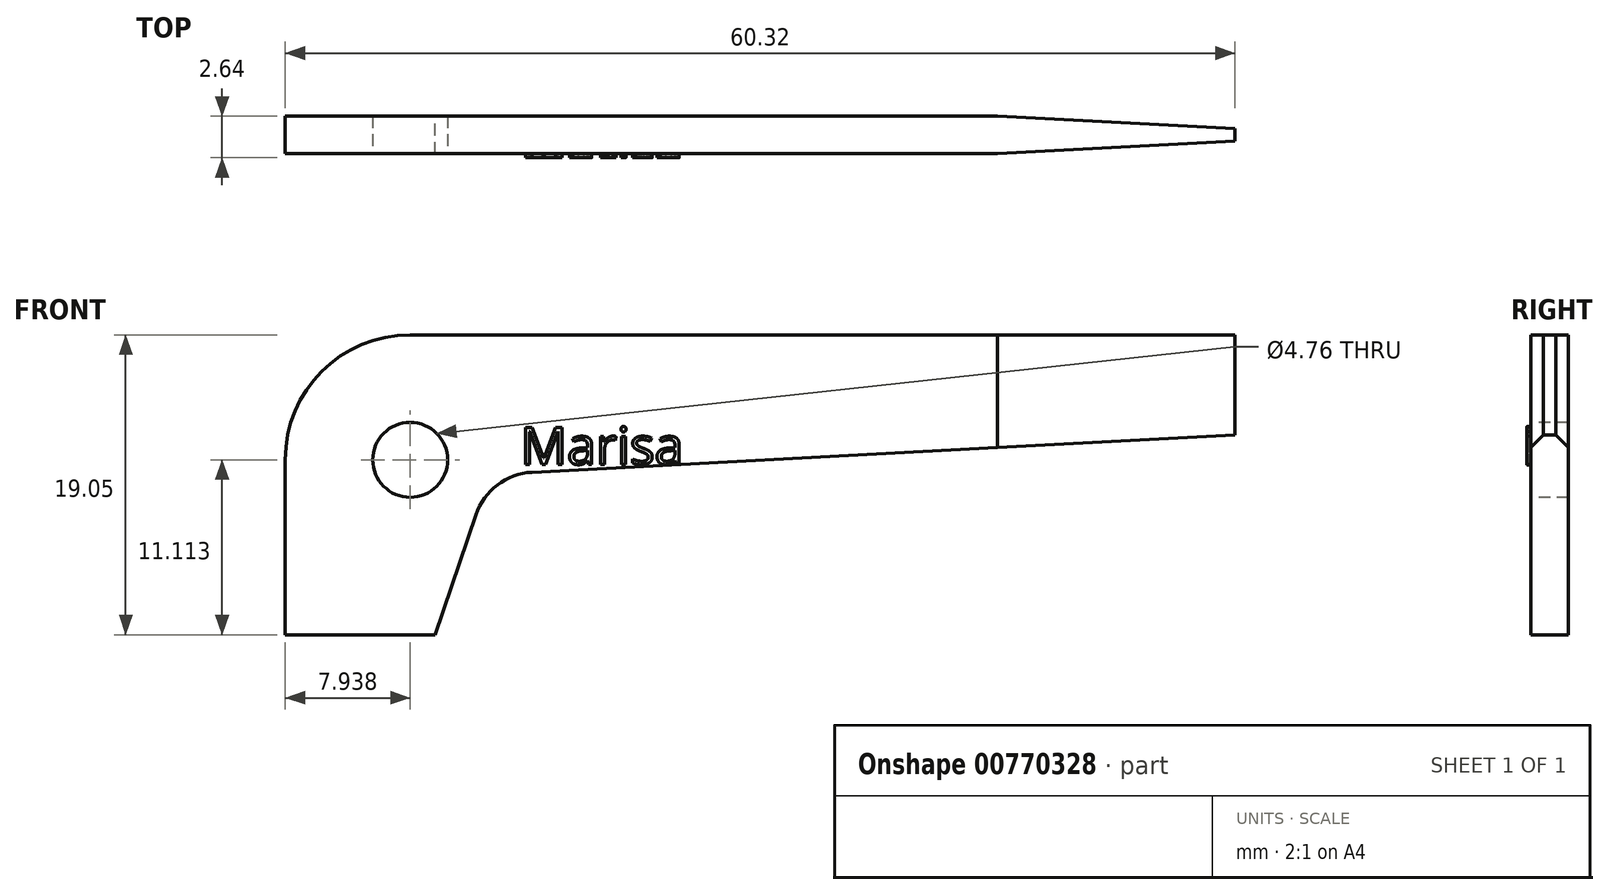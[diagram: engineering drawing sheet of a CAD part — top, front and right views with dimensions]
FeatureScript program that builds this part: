
annotation { "Feature Type Name" : "Feature", "Feature Type Description" : "" }
export const myFeature = defineFeature(function(context is Context, id is Id, definition is map)
    precondition{}
    {
        {
            var Q0;
            Q0=qCreatedBy(makeId("Front.planeOp"),FACE);
            var sketch = newSketch(context, id + "F0", { "sketchPlane" : qUnion([Q0])});
            skLineSegment(sketch, "E0.top", {"start": v(7.94, 19.05) * mm, "end": v(60.33, 19.05) * mm});
            skLineSegment(sketch, "E0.left", {"start": v(0, 0) * mm, "end": v(0, 11.11) * mm});
            skLineSegment(sketch, "E1", {"start": v(9.52, 0) * mm, "end": v(12.11, 7.63) * mm});
            skLineSegment(sketch, "E2", {"start": v(60.33, 12.7) * mm, "end": v(15.66, 10.32) * mm});
            skLineSegment(sketch, "E3", {"start": v(9.52, 0) * mm, "end": v(0, 0) * mm});
            skLineSegment(sketch, "E4", {"start": v(60.33, 12.7) * mm, "end": v(60.33, 19.05) * mm});
            skArc(sketch, "E5", {"start": v(15.66, 10.32) * mm, "mid": v(13.47, 9.52) * mm, "end": v(12.11, 7.63) * mm});
            skPoint(sketch, "E6.visualSharp", {"position": v(0, 19.05) * mm});
            skArc(sketch, "E6.filletArc", {"start": v(7.94, 19.05) * mm, "mid": v(2.32, 16.73) * mm, "end": v(0, 11.11) * mm});
            skSolve(sketch);
        }
        {
            var Q0;
            Q0 = qSketchRegion(id + "F0", true);
            extrude(context, id + "F1", {"entities" : qUnion([Q0]), "depth" : 2.38 * mm, "offsetDistance" : 25.4 * mm});
        }
        {
            var Q0;
            Q0=makeQuery(id+"F1.opExtrude","CAP_FACE",FACE,{"disambiguationData":[OSD([sQuery(id+"F0.wireOp",EDGE,"E0.top"),sQuery(id+"F0.wireOp",EDGE,"E0.left"),sQuery(id+"F0.wireOp",EDGE,"E1"),sQuery(id+"F0.wireOp",EDGE,"E2"),sQuery(id+"F0.wireOp",EDGE,"E3"),sQuery(id+"F0.wireOp",EDGE,"E4"),sQuery(id+"F0.wireOp",EDGE,"E5"),sQuery(id+"F0.wireOp",EDGE,"E6.filletArc")])],"isStart":false});
            var sketch = newSketch(context, id + "F2", { "sketchPlane" : qUnion([Q0])});
            skCircle(sketch, "E7", {"center": v(7.94, 11.11) * mm, "radius": 2.38 * mm});
            skSolve(sketch);
        }
        {
            var Q0;
            Q0=makeQuery(id+"F2.imprint","IMPRINT",FACE,{"disambiguationData":[TD([[makeQuery(id+"F2.imprint","IMPRINT",EDGE,{"derivedFrom":sQuery(id+"F2.wireOp",EDGE,"E7")}),1.0]])]});
            extrude(context, id + "F3", {"entities" : qUnion([Q0]), "operationType" : NewBodyOperationType.REMOVE, "oppositeDirection" : true, "depth" : 25.4 * mm, "offsetDistance" : 25.4 * mm});
        }
        {
            var Q0;
            Q0=makeQuery(id+"F1.opExtrude","SWEPT_FACE",FACE,{"disambiguationData":[OSD([sQuery(id+"F0.wireOp",EDGE,"E0.top")])]});
            var sketch = newSketch(context, id + "F4", { "sketchPlane" : qUnion([Q0])});
            skLineSegment(sketch, "E8", {"start": v(45.24, 0) * mm, "end": v(60.33, -0.8) * mm});
            skLineSegment(sketch, "E9", {"start": v(60.33, -0.8) * mm, "end": v(60.33, 0) * mm});
            skLineSegment(sketch, "E10", {"start": v(60.33, 0) * mm, "end": v(45.24, 0) * mm});
            skLineSegment(sketch, "E11.MirrorCS", {"start": v(45.24, -2.38) * mm, "end": v(60.33, -1.59) * mm});
            skLineSegment(sketch, "E12.MirrorCS", {"start": v(60.33, -2.38) * mm, "end": v(45.24, -2.38) * mm});
            skSolve(sketch);
        }
        {
            var Q0;
            {var subQ0=sQuery(id+"F4.wireOp",EDGE,"E11.MirrorCS");Q0=makeQuery(id+"F4.imprint","IMPRINT",FACE,{"disambiguationData":[TD([[makeQuery(id+"F4.imprint","IMPRINT",EDGE,{"derivedFrom":subQ0}),-1.0]])]});}
            var Q1;
            Q1=makeQuery(id+"F4.imprint","IMPRINT",FACE,{"disambiguationData":[TD([[makeQuery(id+"F4.imprint","IMPRINT",EDGE,{"derivedFrom":sQuery(id+"F4.wireOp",EDGE,"E8")}),1.0]])]});
            extrude(context, id + "F5", {"entities" : qUnion([Q0, Q1]), "operationType" : NewBodyOperationType.REMOVE, "oppositeDirection" : true, "depth" : 25.4 * mm, "offsetDistance" : 25.4 * mm});
        }
        {
            var Q0;
            Q0=makeQuery(id+"F1.opExtrude","CAP_FACE",FACE,{"disambiguationData":[OSD([sQuery(id+"F0.wireOp",EDGE,"E0.top"),sQuery(id+"F0.wireOp",EDGE,"E0.left"),sQuery(id+"F0.wireOp",EDGE,"E1"),sQuery(id+"F0.wireOp",EDGE,"E2"),sQuery(id+"F0.wireOp",EDGE,"E3"),sQuery(id+"F0.wireOp",EDGE,"E4"),sQuery(id+"F0.wireOp",EDGE,"E5"),sQuery(id+"F0.wireOp",EDGE,"E6.filletArc")])],"isStart":false});
            var sketch = newSketch(context, id + "F6", { "sketchPlane" : qUnion([Q0])});
            skText(sketch, "E13", { "text": "Marisa \n", "fontName": "OpenSans-Regular.ttf"});
            const initialGuessF6  = {"E13": [0.01495, 0.01083, 1, 0, 0.00236]};
            skSetInitialGuess(sketch, initialGuessF6);
            skSolve(sketch);
        }
        {
            var Q0;
            Q0 = qSketchRegion(id + "F6", true);
            extrude(context, id + "F7", {"entities" : qUnion([Q0]), "operationType" : NewBodyOperationType.ADD, "depth" : 0.25 * mm, "offsetDistance" : 25.4 * mm});
        }
    });
